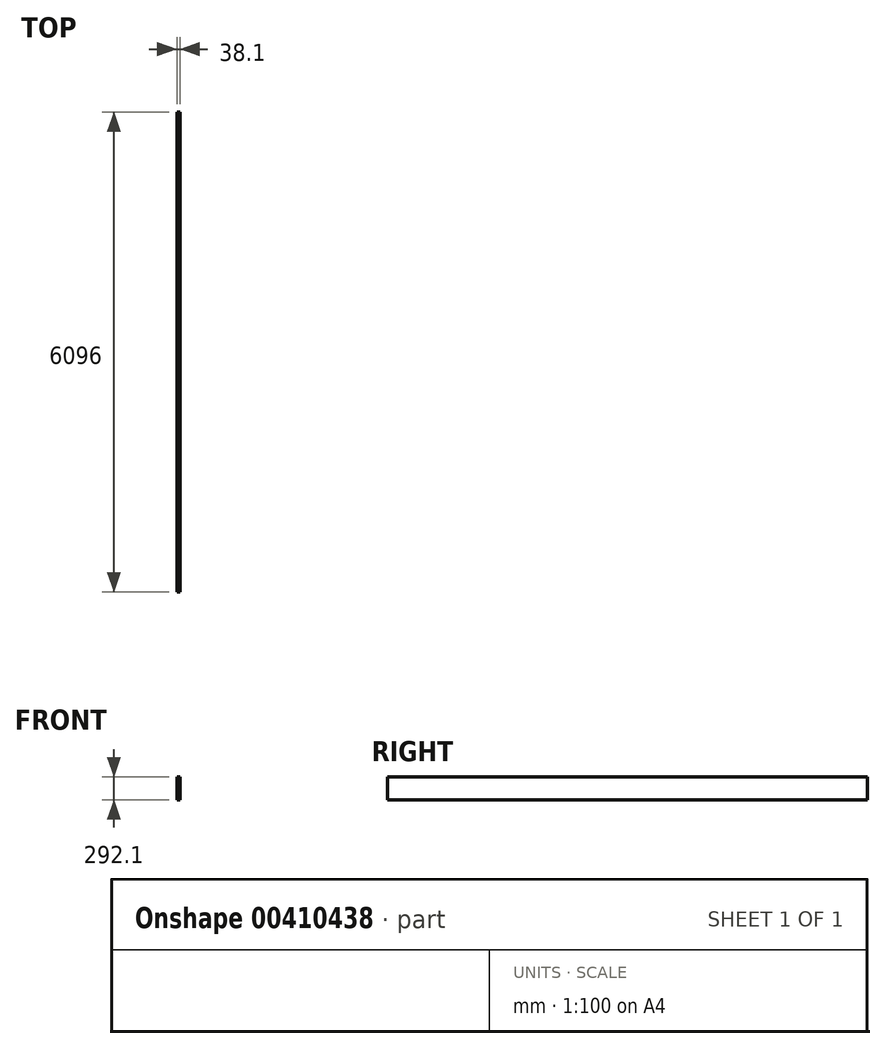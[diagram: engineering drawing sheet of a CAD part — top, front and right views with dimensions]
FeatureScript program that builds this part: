
annotation { "Feature Type Name" : "Feature", "Feature Type Description" : "" }
export const myFeature = defineFeature(function(context is Context, id is Id, definition is map)
    precondition{}
    {
        {
            var Q0;
            Q0=qCreatedBy(makeId("Right.planeOp"),FACE);
            var sketch = newSketch(context, id + "F0", { "sketchPlane" : qUnion([Q0])});
            skLineSegment(sketch, "E0.bottom", {"start": v(-3048, 146.05) * mm, "end": v(3048, 146.05) * mm});
            skLineSegment(sketch, "E0.top", {"start": v(-3048, -146.05) * mm, "end": v(3048, -146.05) * mm});
            skLineSegment(sketch, "E0.left", {"start": v(-3048, 146.05) * mm, "end": v(-3048, -146.05) * mm});
            skLineSegment(sketch, "E0.right", {"start": v(3048, 146.05) * mm, "end": v(3048, -146.05) * mm});
            skPoint(sketch, "E0.middle", {"position": v(0, 0) * mm});
            skSolve(sketch);
        }
        {
            var Q0;
            Q0=qSketchRegion(id+"F0",true);
            extrude(context, id + "F1", {"entities" : qUnion([Q0]), "depth" : 38.1 * mm, "offsetDistance" : 25.4 * mm});
        }
    });
